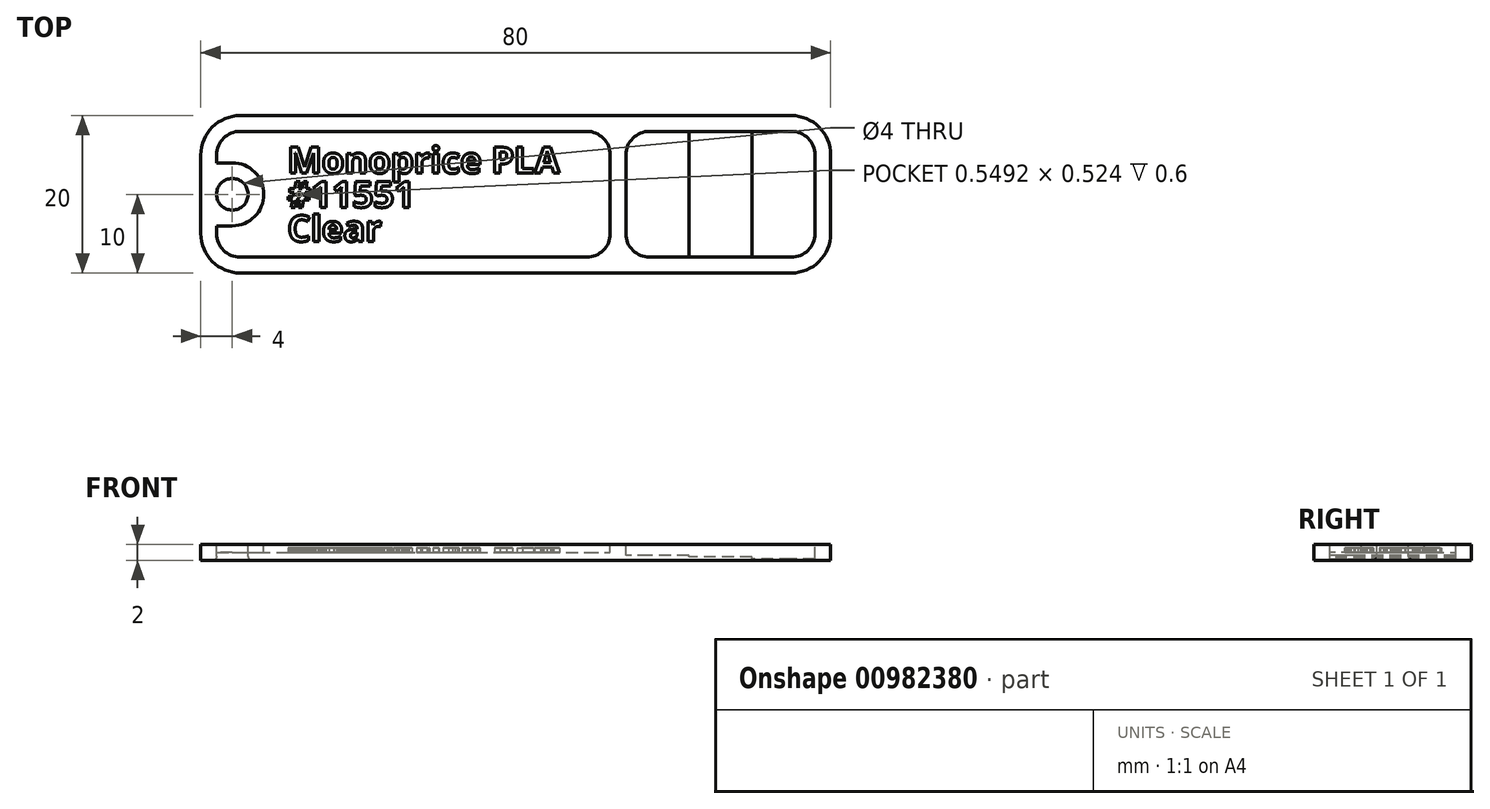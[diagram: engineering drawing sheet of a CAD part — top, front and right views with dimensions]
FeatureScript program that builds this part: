
annotation { "Feature Type Name" : "Feature", "Feature Type Description" : "" }
export const myFeature = defineFeature(function(context is Context, id is Id, definition is map)
    precondition{}
    {
        {
            var Q0;
            Q0=qCreatedBy(makeId("Top.planeOp"),FACE);
            var sketch = newSketch(context, id + "F0", { "sketchPlane" : qUnion([Q0])});
            skLineSegment(sketch, "E0.bottom", {"start": v(35, 10) * mm, "end": v(-35, 10) * mm});
            skLineSegment(sketch, "E0.top", {"start": v(35, -10) * mm, "end": v(-35, -10) * mm});
            skLineSegment(sketch, "E0.left", {"start": v(40, 5) * mm, "end": v(40, -5) * mm});
            skLineSegment(sketch, "E0.right", {"start": v(-40, 5) * mm, "end": v(-40, -5) * mm});
            skPoint(sketch, "E0.middle", {"position": v(0, 0) * mm});
            skPoint(sketch, "E1.visualSharp", {"position": v(-40, 10) * mm});
            skArc(sketch, "E1.filletArc", {"start": v(-35, 10) * mm, "mid": v(-38.54, 8.54) * mm, "end": v(-40, 5) * mm});
            skPoint(sketch, "E2.visualSharp", {"position": v(40, 10) * mm});
            skArc(sketch, "E2.filletArc", {"start": v(40, 5) * mm, "mid": v(38.54, 8.54) * mm, "end": v(35, 10) * mm});
            skPoint(sketch, "E3.visualSharp", {"position": v(40, -10) * mm});
            skArc(sketch, "E3.filletArc", {"start": v(35, -10) * mm, "mid": v(38.54, -8.54) * mm, "end": v(40, -5) * mm});
            skPoint(sketch, "E4.visualSharp", {"position": v(-40, -10) * mm});
            skArc(sketch, "E4.filletArc", {"start": v(-40, -5) * mm, "mid": v(-38.54, -8.54) * mm, "end": v(-35, -10) * mm});
            skSolve(sketch);
        }
        {
            var Q0;
            Q0=qSketchRegion(id+"F0",true);
            extrude(context, id + "F1", {"entities" : qUnion([Q0]), "offsetDistance" : 25 * mm, "depth" : 2 * mm});
        }
        {
            var Q0;
            Q0=makeQuery(id+"F1.opExtrude","CAP_FACE",FACE,{"disambiguationData":[OSD([sQuery(id+"F0.wireOp",EDGE,"E0.bottom"),sQuery(id+"F0.wireOp",EDGE,"E0.top"),sQuery(id+"F0.wireOp",EDGE,"E0.left"),sQuery(id+"F0.wireOp",EDGE,"E0.right"),sQuery(id+"F0.wireOp",EDGE,"E1.filletArc"),sQuery(id+"F0.wireOp",EDGE,"E2.filletArc"),sQuery(id+"F0.wireOp",EDGE,"E3.filletArc"),sQuery(id+"F0.wireOp",EDGE,"E4.filletArc")])],"isStart":false});
            var sketch = newSketch(context, id + "F2", { "sketchPlane" : qUnion([Q0])});
            skLineSegment(sketch, "E5.0", {"start": v(38, -5) * mm, "end": v(38, 5) * mm});
            skArc(sketch, "E5.1", {"start": v(35, -8) * mm, "mid": v(37.12, -7.12) * mm, "end": v(38, -5) * mm});
            skArc(sketch, "E5.2", {"start": v(38, 5) * mm, "mid": v(37.12, 7.12) * mm, "end": v(35, 8) * mm});
            skLineSegment(sketch, "E5.3", {"start": v(-35, -8) * mm, "end": v(9, -8) * mm});
            skLineSegment(sketch, "E5.4", {"start": v(35, 8) * mm, "end": v(17, 8) * mm});
            skArc(sketch, "E5.5", {"start": v(-35, 8) * mm, "mid": v(-37.12, 7.12) * mm, "end": v(-38, 5) * mm});
            skArc(sketch, "E5.7", {"start": v(-38, -5) * mm, "mid": v(-37.12, -7.12) * mm, "end": v(-35, -8) * mm});
            skCircle(sketch, "E6", {"center": v(-36, 0) * mm, "radius": 2 * mm, "construction": true});
            skArc(sketch, "E7.0", {"start": v(-36, -4) * mm, "mid": v(-32, 0) * mm, "end": v(-36, 4) * mm});
            skLineSegment(sketch, "E8", {"start": v(-38, -5) * mm, "end": v(-38, -4) * mm});
            skLineSegment(sketch, "E9", {"start": v(-36, 4) * mm, "end": v(-38, 4) * mm});
            skLineSegment(sketch, "E10", {"start": v(-36, -4) * mm, "end": v(-38, -4) * mm});
            skLineSegment(sketch, "E11.trimOffspring", {"start": v(-38, 4) * mm, "end": v(-38, 5) * mm});
            skArc(sketch, "E12", {"start": v(17, 8) * mm, "mid": v(14.88, 7.12) * mm, "end": v(14, 5) * mm});
            skArc(sketch, "E13", {"start": v(14, -5) * mm, "mid": v(14.88, -7.12) * mm, "end": v(17, -8) * mm});
            skLineSegment(sketch, "E14", {"start": v(14, -5) * mm, "end": v(14, 5) * mm});
            skArc(sketch, "E15", {"start": v(12, 5) * mm, "mid": v(11.12, 7.12) * mm, "end": v(9, 8) * mm});
            skArc(sketch, "E16", {"start": v(12, -5) * mm, "mid": v(11.12, -7.12) * mm, "end": v(9, -8) * mm});
            skLineSegment(sketch, "E17", {"start": v(12, -5) * mm, "end": v(12, 5) * mm});
            skLineSegment(sketch, "E18.trimOffspring", {"start": v(9, 8) * mm, "end": v(-35, 8) * mm});
            skLineSegment(sketch, "E19.trimOffspring", {"start": v(17, -8) * mm, "end": v(35, -8) * mm});
            skSolve(sketch);
        }
        {
            var Q0;
            Q0=qSketchRegion(id+"F2",true);
            extrude(context, id + "F3", {"entities" : qUnion([Q0]), "operationType" : NewBodyOperationType.REMOVE, "oppositeDirection" : true, "offsetDistance" : 25 * mm, "depth" : 1 * mm});
        }
        {
            var Q0;
            Q0=makeQuery(id+"F1.opExtrude","CAP_FACE",FACE,{"disambiguationData":[OSD([sQuery(id+"F0.wireOp",EDGE,"E0.bottom"),sQuery(id+"F0.wireOp",EDGE,"E0.top"),sQuery(id+"F0.wireOp",EDGE,"E0.left"),sQuery(id+"F0.wireOp",EDGE,"E0.right"),sQuery(id+"F0.wireOp",EDGE,"E1.filletArc"),sQuery(id+"F0.wireOp",EDGE,"E2.filletArc"),sQuery(id+"F0.wireOp",EDGE,"E3.filletArc"),sQuery(id+"F0.wireOp",EDGE,"E4.filletArc")])],"isStart":false});
            var sketch = newSketch(context, id + "F4", { "sketchPlane" : qUnion([Q0])});
            skCircle(sketch, "E20.0", {"center": v(-36, 0) * mm, "radius": 2 * mm});
            skSolve(sketch);
        }
        {
            var Q0;
            Q0=qSketchRegion(id+"F4",true);
            extrude(context, id + "F5", {"entities" : qUnion([Q0]), "operationType" : NewBodyOperationType.REMOVE, "endBound" : BoundingType.THROUGH_ALL, "oppositeDirection" : true, "depth" : 25 * mm});
        }
        {
            var Q0;
            Q0=makeQuery(id+"F5.boolean.opBoolean","COPY",EDGE,{"derivedFrom":makeQuery(id+"F5.opExtrude","CAP_EDGE",EDGE,{"disambiguationData":[OSD([sQuery(id+"F4.wireOp",EDGE,"E20.0")])],"isStart":true})});
            var Q1;
            Q1=makeQuery(id+"F5.boolean.opBoolean","INTERSECT",EDGE,{"derivedFrom":[makeQuery(id+"F1.opExtrude","CAP_FACE",FACE,{"disambiguationData":[OSD([sQuery(id+"F0.wireOp",EDGE,"E0.bottom"),sQuery(id+"F0.wireOp",EDGE,"E0.top"),sQuery(id+"F0.wireOp",EDGE,"E0.left"),sQuery(id+"F0.wireOp",EDGE,"E0.right"),sQuery(id+"F0.wireOp",EDGE,"E1.filletArc"),sQuery(id+"F0.wireOp",EDGE,"E2.filletArc"),sQuery(id+"F0.wireOp",EDGE,"E3.filletArc"),sQuery(id+"F0.wireOp",EDGE,"E4.filletArc")])],"isStart":true}),makeQuery(id+"F5.opExtrude","SWEPT_FACE",FACE,{"disambiguationData":[OSD([sQuery(id+"F4.wireOp",EDGE,"E20.0")])]})]});
            fillet(context, id + "F6", {"entities" : qUnion([Q0, Q1]), "radius" : .5 * mm, "tangentPropagation" : true, "allowEdgeOverflow" : false});
        }
        {
            var Q0;
            Q0=makeQuery(id+"F3.boolean.opBoolean","COPY",FACE,{"derivedFrom":makeQuery(id+"F3.opExtrude","CAP_FACE",FACE,{"disambiguationData":[OSD([sQuery(id+"F2.wireOp",EDGE,"E5.0"),sQuery(id+"F2.wireOp",EDGE,"E5.1"),sQuery(id+"F2.wireOp",EDGE,"E5.2"),sQuery(id+"F2.wireOp",EDGE,"E5.4"),sQuery(id+"F2.wireOp",EDGE,"E12"),sQuery(id+"F2.wireOp",EDGE,"E13"),sQuery(id+"F2.wireOp",EDGE,"E14"),sQuery(id+"F2.wireOp",EDGE,"E19.trimOffspring")])],"isStart":false})});
            extrude(context, id + "F7", {"entities" : qUnion([Q0]), "operationType" : NewBodyOperationType.REMOVE, "oppositeDirection" : true, "offsetDistance" : 25 * mm, "depth" : 0.4 * mm});
        }
        {
            var Q0;
            Q0=makeQuery(id+"F7.boolean.opBoolean","COPY",FACE,{"derivedFrom":makeQuery(id+"F7.opExtrude","CAP_FACE",FACE,{"disambiguationData":[OSD([sQuery(id+"F2.wireOp",EDGE,"E5.0"),sQuery(id+"F2.wireOp",EDGE,"E5.1"),sQuery(id+"F2.wireOp",EDGE,"E5.2"),sQuery(id+"F2.wireOp",EDGE,"E5.4"),sQuery(id+"F2.wireOp",EDGE,"E12"),sQuery(id+"F2.wireOp",EDGE,"E13"),sQuery(id+"F2.wireOp",EDGE,"E14"),sQuery(id+"F2.wireOp",EDGE,"E19.trimOffspring")])],"isStart":false})});
            var sketch = newSketch(context, id + "F8", { "sketchPlane" : qUnion([Q0])});
            skArc(sketch, "E21.0.0", {"start": v(35, -8) * mm, "mid": v(37.12, -7.12) * mm, "end": v(38, -5) * mm});
            skLineSegment(sketch, "E21.0.1", {"start": v(38, -5) * mm, "end": v(38, 5) * mm});
            skArc(sketch, "E21.0.2", {"start": v(38, 5) * mm, "mid": v(37.12, 7.12) * mm, "end": v(35, 8) * mm});
            skLineSegment(sketch, "E21.0.3", {"start": v(35, 8) * mm, "end": v(22, 8) * mm});
            skLineSegment(sketch, "E21.0.7", {"start": v(22, -8) * mm, "end": v(35, -8) * mm});
            skLineSegment(sketch, "E22", {"start": v(22, 8) * mm, "end": v(22, -8) * mm});
            skPoint(sketch, "E21.0.4.start.orphan", {"position": v(17, 8) * mm});
            skPoint(sketch, "E21.0.5.start.orphan", {"position": v(14, 5) * mm});
            skPoint(sketch, "E21.0.6.start.orphan", {"position": v(14, -5) * mm});
            skPoint(sketch, "E23.orphan", {"position": v(17, -8) * mm});
            skSolve(sketch);
        }
        {
            var Q0;
            Q0=qSketchRegion(id+"F8",true);
            extrude(context, id + "F9", {"entities" : qUnion([Q0]), "operationType" : NewBodyOperationType.REMOVE, "oppositeDirection" : true, "offsetDistance" : 25 * mm, "depth" : 0.2 * mm});
        }
        {
            var Q0;
            Q0=makeQuery(id+"F9.boolean.opBoolean","COPY",FACE,{"derivedFrom":makeQuery(id+"F9.opExtrude","CAP_FACE",FACE,{"disambiguationData":[OSD([sQuery(id+"F8.wireOp",EDGE,"E21.0.0"),sQuery(id+"F8.wireOp",EDGE,"E21.0.1"),sQuery(id+"F8.wireOp",EDGE,"E21.0.2"),sQuery(id+"F8.wireOp",EDGE,"E21.0.3"),sQuery(id+"F8.wireOp",EDGE,"E21.0.7"),sQuery(id+"F8.wireOp",EDGE,"E22")])],"isStart":false})});
            var sketch = newSketch(context, id + "F10", { "sketchPlane" : qUnion([Q0])});
            skLineSegment(sketch, "E24.0.0", {"start": v(35, 8) * mm, "end": v(30, 8) * mm});
            skLineSegment(sketch, "E24.0.2", {"start": v(30, -8) * mm, "end": v(35, -8) * mm});
            skArc(sketch, "E24.0.3", {"start": v(35, -8) * mm, "mid": v(37.12, -7.12) * mm, "end": v(38, -5) * mm});
            skLineSegment(sketch, "E24.0.4", {"start": v(38, -5) * mm, "end": v(38, 5) * mm});
            skArc(sketch, "E24.0.5", {"start": v(38, 5) * mm, "mid": v(37.12, 7.12) * mm, "end": v(35, 8) * mm});
            skLineSegment(sketch, "E25", {"start": v(30, 8) * mm, "end": v(30, -8) * mm});
            skPoint(sketch, "E24.0.1.end.orphan", {"position": v(22, -8) * mm});
            skPoint(sketch, "E26.orphan", {"position": v(22, 8) * mm});
            skSolve(sketch);
        }
        {
            var Q0;
            Q0=makeQuery(id+"F10.imprint","IMPRINT",FACE,{"disambiguationData":[TD([[makeQuery(id+"F10.imprint","IMPRINT",EDGE,{"derivedFrom":sQuery(id+"F10.wireOp",EDGE,"E24.0.0")}),1.0]])]});
            extrude(context, id + "F11", {"entities" : qUnion([Q0]), "operationType" : NewBodyOperationType.REMOVE, "oppositeDirection" : true, "offsetDistance" : 25 * mm, "depth" : 0.2 * mm});
        }
        {
            var Q0;
            Q0=makeQuery(id+"F3.boolean.opBoolean","COPY",FACE,{"derivedFrom":makeQuery(id+"F3.opExtrude","CAP_FACE",FACE,{"disambiguationData":[OSD([sQuery(id+"F2.wireOp",EDGE,"E5.3"),sQuery(id+"F2.wireOp",EDGE,"E5.5"),sQuery(id+"F2.wireOp",EDGE,"E5.7"),sQuery(id+"F2.wireOp",EDGE,"E7.0"),sQuery(id+"F2.wireOp",EDGE,"E8"),sQuery(id+"F2.wireOp",EDGE,"E9"),sQuery(id+"F2.wireOp",EDGE,"E10"),sQuery(id+"F2.wireOp",EDGE,"E11.trimOffspring"),sQuery(id+"F2.wireOp",EDGE,"E15"),sQuery(id+"F2.wireOp",EDGE,"E16"),sQuery(id+"F2.wireOp",EDGE,"E17"),sQuery(id+"F2.wireOp",EDGE,"E18.trimOffspring")])],"isStart":false})});
            var sketch = newSketch(context, id + "F12", { "sketchPlane" : qUnion([Q0])});
            skText(sketch, "E27", { "text": "Monoprice PLA", "fontName": "OpenSans-Bold.ttf"});
            skText(sketch, "E28", { "text": "#11551", "fontName": "OpenSans-Bold.ttf"});
            skText(sketch, "E29", { "text": "Clear", "fontName": "OpenSans-Bold.ttf"});
            skLineSegment(sketch, "E30", {"start": v(-27.83, 1.67) * mm, "end": v(-27.83, 2.67) * mm, "construction": true});
            skLineSegment(sketch, "E31", {"start": v(-26.66, -2.67) * mm, "end": v(-26.66, -1.67) * mm, "construction": true});
            skLineSegment(sketch, "E32.bottom", {"start": v(-31, 7) * mm, "end": v(10, 7) * mm, "construction": true});
            skLineSegment(sketch, "E32.top", {"start": v(-31, -7) * mm, "end": v(10, -7) * mm, "construction": true});
            skLineSegment(sketch, "E32.left", {"start": v(-31, 7) * mm, "end": v(-31, -7) * mm, "construction": true});
            skLineSegment(sketch, "E32.right", {"start": v(10, 7) * mm, "end": v(10, -7) * mm, "construction": true});
            skLineSegment(sketch, "E33", {"start": v(-13.47, 7) * mm, "end": v(-13.47, 8) * mm, "construction": true});
            skLineSegment(sketch, "E34", {"start": v(-13.67, -7) * mm, "end": v(-13.67, -8) * mm, "construction": true});
            skLineSegment(sketch, "E35", {"start": v(-32, 0) * mm, "end": v(-31, 0) * mm, "construction": true});
            skPoint(sketch, "E35.startSnap0", {"position": v(-31, 0) * mm});
            skLineSegment(sketch, "E36", {"start": v(-29, 4.33) * mm, "end": v(-31, 4.33) * mm, "construction": true});
            skLineSegment(sketch, "E37", {"start": v(10, 1.23) * mm, "end": v(12, 1.23) * mm, "construction": true});
            skLineSegment(sketch, "E38", {"start": v(-29, -0.54) * mm, "end": v(-31, -0.54) * mm, "construction": true});
            skLineSegment(sketch, "E39", {"start": v(-29, -4.33) * mm, "end": v(-31, -4.33) * mm, "construction": true});
            skLineSegment(sketch, "E40", {"start": v(-25.76, 6) * mm, "end": v(-25.76, 7) * mm, "construction": true});
            skLineSegment(sketch, "E41", {"start": v(-26.93, -6) * mm, "end": v(-26.93, -7) * mm, "construction": true});
            const initialGuessF12  = {"E27": [-0.029, 0.00267, 1, 0, 0.00333], "E28": [-0.029, -0.00167, 1, 0, 0.00333], "E29": [-0.029, -0.006, 1, 0, 0.00333]};
            skSetInitialGuess(sketch, initialGuessF12);
            skSolve(sketch);
        }
        {
            var Q0;
            Q0=qSketchRegion(id+"F12",true);
            extrude(context, id + "F13", {"entities" : qUnion([Q0]), "operationType" : NewBodyOperationType.ADD, "depth" : 0.6 * mm, "offsetDistance" : 25 * mm});
        }
    });
